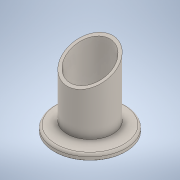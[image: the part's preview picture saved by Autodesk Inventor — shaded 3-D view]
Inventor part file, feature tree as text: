
AUTODESK INVENTOR PART (.ipt)
format: ipt  version: 2021 (Build 250183000, 183)  size: 157,696 bytes
history: native  units: in
note: dims shown in document units (in); Inventor stores cm internally (conversion verified against a paired STEP export)
features: extrude x1, sketch x1, other x1
ambient origin geometry x8: Origin, YZ Plane, XZ Plane, XY Plane, X Axis, Y Axis, Z Axis, Center Point
bodies: Solid1 (feature_tree)
feature tree (3):
  extrude  "Extrusion1"  TaperAngle=0.0deg  [1 undecoded]
  sketch  "Sketch1"  dims[d0=0.1718in d1=0.0in d2=0.0in]
  parser-record x1  (decoder bookkeeping rows leaked as tree rows — omitted from the tree; the rows remain in map.json)
note: 1 required parameter value undecoded (feature->parameter linkage not recoverable at this tier; creation-order binding heuristic only, values carry confidence <= 0.55)
